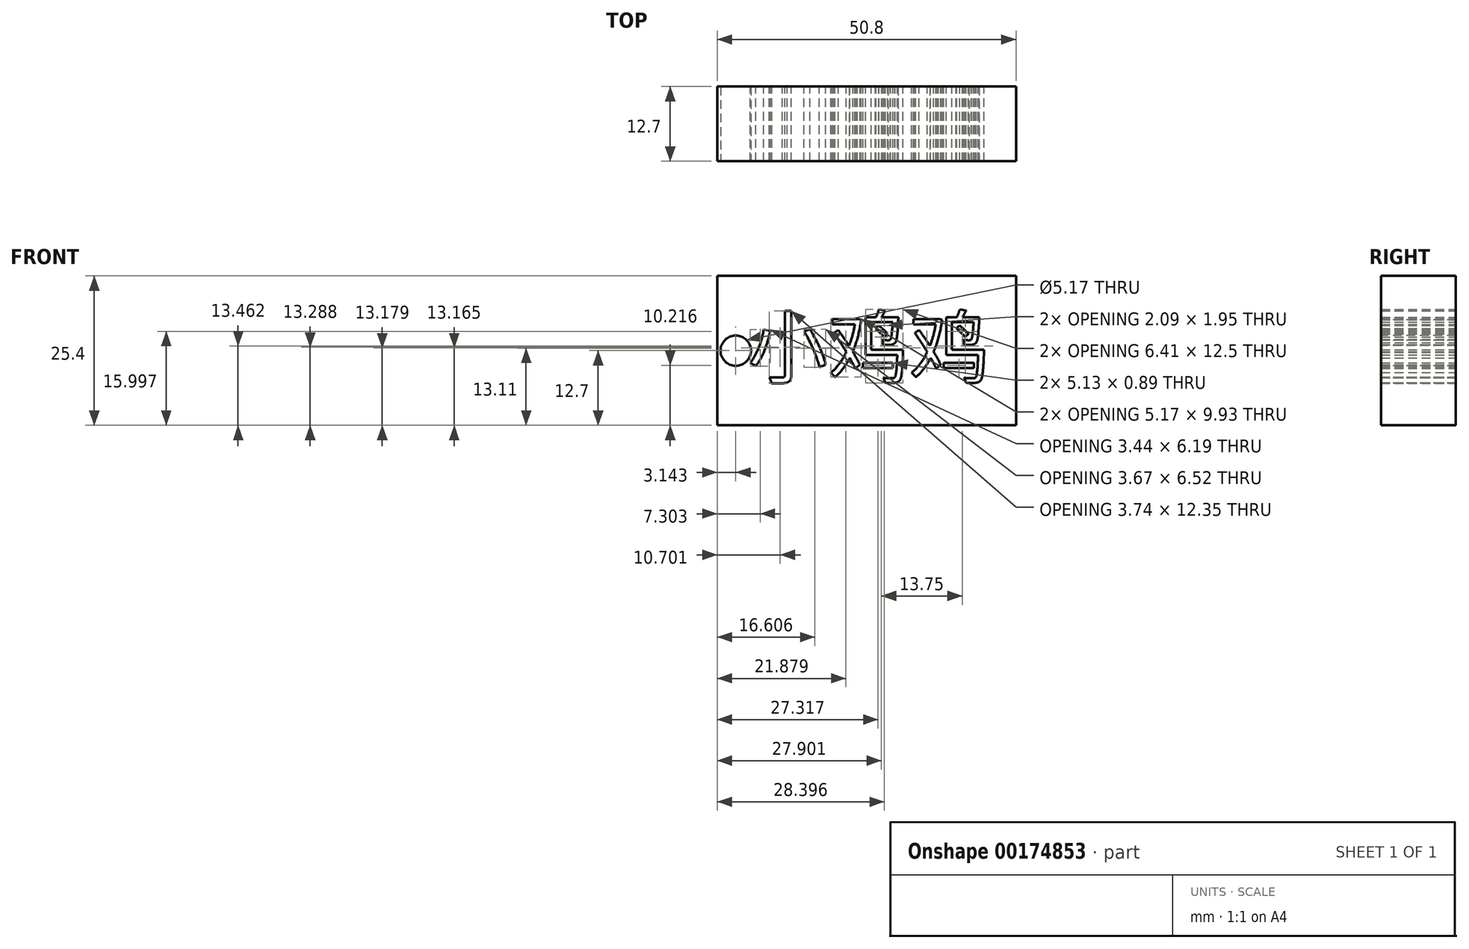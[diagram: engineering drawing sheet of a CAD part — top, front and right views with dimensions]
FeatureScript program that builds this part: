
annotation { "Feature Type Name" : "Feature", "Feature Type Description" : "" }
export const myFeature = defineFeature(function(context is Context, id is Id, definition is map)
    precondition{}
    {
        {
            var Q0;
            Q0=qCreatedBy(makeId("Front.planeOp"),FACE);
            var sketch = newSketch(context, id + "F0", { "sketchPlane" : qUnion([Q0])});
            skLineSegment(sketch, "E0.bottom", {"start": v(-25.4, 12.7) * mm, "end": v(25.4, 12.7) * mm});
            skLineSegment(sketch, "E0.top", {"start": v(-25.4, -12.7) * mm, "end": v(25.4, -12.7) * mm});
            skLineSegment(sketch, "E0.left", {"start": v(-25.4, 12.7) * mm, "end": v(-25.4, -12.7) * mm});
            skLineSegment(sketch, "E0.right", {"start": v(25.4, 12.7) * mm, "end": v(25.4, -12.7) * mm});
            skText(sketch, "E1", { "text": "小鸡鸡", "fontName": "NotoSansCJKsc-Regular.otf"});
            const initialGuessF0  = {"E1": [-0.02031, -0.00454, 1, 0, 0.0099]};
            skSetInitialGuess(sketch, initialGuessF0);
            skSolve(sketch);
        }
        {
            var Q0;
            Q0=makeQuery(id+"F0.imprint","IMPRINT",FACE,{"disambiguationData":[TD([[makeQuery(id+"F0.imprint","IMPRINT",EDGE,{"derivedFrom":sQuery(id+"F0.wireOp",EDGE,"E0.bottom")}),-1.0]])]});
            extrude(context, id + "F1", {"entities" : qUnion([Q0]), "depth" : 12.7 * mm});
        }
        {
            var Q0;
            Q0=makeQuery(id+"F1.opExtrude","CAP_FACE",FACE,{"disambiguationData":[OSD([sQuery(id+"F0.wireOp",EDGE,"E0.bottom"),sQuery(id+"F0.wireOp",EDGE,"E0.top"),sQuery(id+"F0.wireOp",EDGE,"E0.left"),sQuery(id+"F0.wireOp",EDGE,"E0.right"),sQuery(id+"F0.wireOp",EDGE,"E1.sketch_text.stroke-0"),sQuery(id+"F0.wireOp",EDGE,"E1.sketch_text.stroke-1"),sQuery(id+"F0.wireOp",EDGE,"E1.sketch_text.stroke-2"),sQuery(id+"F0.wireOp",EDGE,"E1.sketch_text.stroke-3"),sQuery(id+"F0.wireOp",EDGE,"E1.sketch_text.stroke-4"),sQuery(id+"F0.wireOp",EDGE,"E1.sketch_text.stroke-5"),sQuery(id+"F0.wireOp",EDGE,"E1.sketch_text.stroke-6"),sQuery(id+"F0.wireOp",EDGE,"E1.sketch_text.stroke-7"),sQuery(id+"F0.wireOp",EDGE,"E1.sketch_text.stroke-8"),sQuery(id+"F0.wireOp",EDGE,"E1.sketch_text.stroke-9"),sQuery(id+"F0.wireOp",EDGE,"E1.sketch_text.stroke-10"),sQuery(id+"F0.wireOp",EDGE,"E1.sketch_text.stroke-11"),sQuery(id+"F0.wireOp",EDGE,"E1.sketch_text.stroke-12"),sQuery(id+"F0.wireOp",EDGE,"E1.sketch_text.stroke-13"),sQuery(id+"F0.wireOp",EDGE,"E1.sketch_text.stroke-14"),sQuery(id+"F0.wireOp",EDGE,"E1.sketch_text.stroke-15"),sQuery(id+"F0.wireOp",EDGE,"E1.sketch_text.stroke-16"),sQuery(id+"F0.wireOp",EDGE,"E1.sketch_text.stroke-17"),sQuery(id+"F0.wireOp",EDGE,"E1.sketch_text.stroke-18"),sQuery(id+"F0.wireOp",EDGE,"E1.sketch_text.stroke-19"),sQuery(id+"F0.wireOp",EDGE,"E1.sketch_text.stroke-20"),sQuery(id+"F0.wireOp",EDGE,"E1.sketch_text.stroke-21"),sQuery(id+"F0.wireOp",EDGE,"E1.sketch_text.stroke-22"),sQuery(id+"F0.wireOp",EDGE,"E1.sketch_text.stroke-23"),sQuery(id+"F0.wireOp",EDGE,"E1.sketch_text.stroke-24"),sQuery(id+"F0.wireOp",EDGE,"E1.sketch_text.stroke-25"),sQuery(id+"F0.wireOp",EDGE,"E1.sketch_text.stroke-26"),sQuery(id+"F0.wireOp",EDGE,"E1.sketch_text.stroke-27"),sQuery(id+"F0.wireOp",EDGE,"E1.sketch_text.stroke-28"),sQuery(id+"F0.wireOp",EDGE,"E1.sketch_text.stroke-29"),sQuery(id+"F0.wireOp",EDGE,"E1.sketch_text.stroke-30"),sQuery(id+"F0.wireOp",EDGE,"E1.sketch_text.stroke-31"),sQuery(id+"F0.wireOp",EDGE,"E1.sketch_text.stroke-32"),sQuery(id+"F0.wireOp",EDGE,"E1.sketch_text.stroke-33"),sQuery(id+"F0.wireOp",EDGE,"E1.sketch_text.stroke-34"),sQuery(id+"F0.wireOp",EDGE,"E1.sketch_text.stroke-35"),sQuery(id+"F0.wireOp",EDGE,"E1.sketch_text.stroke-36"),sQuery(id+"F0.wireOp",EDGE,"E1.sketch_text.stroke-37"),sQuery(id+"F0.wireOp",EDGE,"E1.sketch_text.stroke-38"),sQuery(id+"F0.wireOp",EDGE,"E1.sketch_text.stroke-39"),sQuery(id+"F0.wireOp",EDGE,"E1.sketch_text.stroke-40"),sQuery(id+"F0.wireOp",EDGE,"E1.sketch_text.stroke-41"),sQuery(id+"F0.wireOp",EDGE,"E1.sketch_text.stroke-42"),sQuery(id+"F0.wireOp",EDGE,"E1.sketch_text.stroke-43"),sQuery(id+"F0.wireOp",EDGE,"E1.sketch_text.stroke-44"),sQuery(id+"F0.wireOp",EDGE,"E1.sketch_text.stroke-45"),sQuery(id+"F0.wireOp",EDGE,"E1.sketch_text.stroke-46"),sQuery(id+"F0.wireOp",EDGE,"E1.sketch_text.stroke-47"),sQuery(id+"F0.wireOp",EDGE,"E1.sketch_text.stroke-48"),sQuery(id+"F0.wireOp",EDGE,"E1.sketch_text.stroke-49"),sQuery(id+"F0.wireOp",EDGE,"E1.sketch_text.stroke-50"),sQuery(id+"F0.wireOp",EDGE,"E1.sketch_text.stroke-51"),sQuery(id+"F0.wireOp",EDGE,"E1.sketch_text.stroke-52"),sQuery(id+"F0.wireOp",EDGE,"E1.sketch_text.stroke-53"),sQuery(id+"F0.wireOp",EDGE,"E1.sketch_text.stroke-54"),sQuery(id+"F0.wireOp",EDGE,"E1.sketch_text.stroke-55"),sQuery(id+"F0.wireOp",EDGE,"E1.sketch_text.stroke-56"),sQuery(id+"F0.wireOp",EDGE,"E1.sketch_text.stroke-57"),sQuery(id+"F0.wireOp",EDGE,"E1.sketch_text.stroke-58"),sQuery(id+"F0.wireOp",EDGE,"E1.sketch_text.stroke-59"),sQuery(id+"F0.wireOp",EDGE,"E1.sketch_text.stroke-60"),sQuery(id+"F0.wireOp",EDGE,"E1.sketch_text.stroke-61"),sQuery(id+"F0.wireOp",EDGE,"E1.sketch_text.stroke-62"),sQuery(id+"F0.wireOp",EDGE,"E1.sketch_text.stroke-63"),sQuery(id+"F0.wireOp",EDGE,"E1.sketch_text.stroke-64"),sQuery(id+"F0.wireOp",EDGE,"E1.sketch_text.stroke-65"),sQuery(id+"F0.wireOp",EDGE,"E1.sketch_text.stroke-66"),sQuery(id+"F0.wireOp",EDGE,"E1.sketch_text.stroke-67"),sQuery(id+"F0.wireOp",EDGE,"E1.sketch_text.stroke-68"),sQuery(id+"F0.wireOp",EDGE,"E1.sketch_text.stroke-69"),sQuery(id+"F0.wireOp",EDGE,"E1.sketch_text.stroke-70"),sQuery(id+"F0.wireOp",EDGE,"E1.sketch_text.stroke-71"),sQuery(id+"F0.wireOp",EDGE,"E1.sketch_text.stroke-72"),sQuery(id+"F0.wireOp",EDGE,"E1.sketch_text.stroke-73"),sQuery(id+"F0.wireOp",EDGE,"E1.sketch_text.stroke-74"),sQuery(id+"F0.wireOp",EDGE,"E1.sketch_text.stroke-75"),sQuery(id+"F0.wireOp",EDGE,"E1.sketch_text.stroke-76"),sQuery(id+"F0.wireOp",EDGE,"E1.sketch_text.stroke-77"),sQuery(id+"F0.wireOp",EDGE,"E1.sketch_text.stroke-78"),sQuery(id+"F0.wireOp",EDGE,"E1.sketch_text.stroke-79"),sQuery(id+"F0.wireOp",EDGE,"E1.sketch_text.stroke-80"),sQuery(id+"F0.wireOp",EDGE,"E1.sketch_text.stroke-81"),sQuery(id+"F0.wireOp",EDGE,"E1.sketch_text.stroke-82"),sQuery(id+"F0.wireOp",EDGE,"E1.sketch_text.stroke-83"),sQuery(id+"F0.wireOp",EDGE,"E1.sketch_text.stroke-84"),sQuery(id+"F0.wireOp",EDGE,"E1.sketch_text.stroke-85"),sQuery(id+"F0.wireOp",EDGE,"E1.sketch_text.stroke-86"),sQuery(id+"F0.wireOp",EDGE,"E1.sketch_text.stroke-87"),sQuery(id+"F0.wireOp",EDGE,"E1.sketch_text.stroke-88"),sQuery(id+"F0.wireOp",EDGE,"E1.sketch_text.stroke-89"),sQuery(id+"F0.wireOp",EDGE,"E1.sketch_text.stroke-90"),sQuery(id+"F0.wireOp",EDGE,"E1.sketch_text.stroke-91"),sQuery(id+"F0.wireOp",EDGE,"E1.sketch_text.stroke-92"),sQuery(id+"F0.wireOp",EDGE,"E1.sketch_text.stroke-93"),sQuery(id+"F0.wireOp",EDGE,"E1.sketch_text.stroke-94"),sQuery(id+"F0.wireOp",EDGE,"E1.sketch_text.stroke-95"),sQuery(id+"F0.wireOp",EDGE,"E1.sketch_text.stroke-96"),sQuery(id+"F0.wireOp",EDGE,"E1.sketch_text.stroke-97"),sQuery(id+"F0.wireOp",EDGE,"E1.sketch_text.stroke-98"),sQuery(id+"F0.wireOp",EDGE,"E1.sketch_text.stroke-99"),sQuery(id+"F0.wireOp",EDGE,"E1.sketch_text.stroke-100"),sQuery(id+"F0.wireOp",EDGE,"E1.sketch_text.stroke-101"),sQuery(id+"F0.wireOp",EDGE,"E1.sketch_text.stroke-102"),sQuery(id+"F0.wireOp",EDGE,"E1.sketch_text.stroke-103"),sQuery(id+"F0.wireOp",EDGE,"E1.sketch_text.stroke-104"),sQuery(id+"F0.wireOp",EDGE,"E1.sketch_text.stroke-105"),sQuery(id+"F0.wireOp",EDGE,"E1.sketch_text.stroke-106"),sQuery(id+"F0.wireOp",EDGE,"E1.sketch_text.stroke-107"),sQuery(id+"F0.wireOp",EDGE,"E1.sketch_text.stroke-108"),sQuery(id+"F0.wireOp",EDGE,"E1.sketch_text.stroke-109"),sQuery(id+"F0.wireOp",EDGE,"E1.sketch_text.stroke-110"),sQuery(id+"F0.wireOp",EDGE,"E1.sketch_text.stroke-111"),sQuery(id+"F0.wireOp",EDGE,"E1.sketch_text.stroke-112"),sQuery(id+"F0.wireOp",EDGE,"E1.sketch_text.stroke-113"),sQuery(id+"F0.wireOp",EDGE,"E1.sketch_text.stroke-114"),sQuery(id+"F0.wireOp",EDGE,"E1.sketch_text.stroke-115")])],"isStart":false});
            var sketch = newSketch(context, id + "F2", { "sketchPlane" : qUnion([Q0])});
            skCircle(sketch, "E2", {"center": v(-22.26, 0) * mm, "radius": 2.59 * mm});
            skSolve(sketch);
        }
        {
            var Q0;
            Q0=makeQuery(id+"F2.imprint","IMPRINT",FACE,{"disambiguationData":[TD([[makeQuery(id+"F2.imprint","IMPRINT",EDGE,{"derivedFrom":sQuery(id+"F2.wireOp",EDGE,"E2")}),1.0]])]});
            var Q1;
            Q1=sQuery(id+"F2.wireOp",EDGE,"E2");
            extrude(context, id + "F3", {"entities" : qUnion([Q0]), "operationType" : NewBodyOperationType.REMOVE, "surfaceEntities" : qUnion([Q1]), "endBound" : BoundingType.THROUGH_ALL, "oppositeDirection" : true, "depth" : 25.4 * mm});
        }
    });
